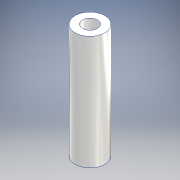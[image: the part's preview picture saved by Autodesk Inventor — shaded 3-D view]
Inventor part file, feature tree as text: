
AUTODESK INVENTOR PART (.ipt)
format: ipt  version: 2016 (Build 200138000, 138)  size: 95,744 bytes
history: native  units: mm
features: other x1, extrude x1, sketch x1
ambient origin geometry x8: Origin, YZ Plane, XZ Plane, XY Plane, X Axis, Y Axis, Z Axis, Center Point
bodies: Body1 (feature_tree)
feature tree (3):
  other  "ソリッド1"
  extrude  "押し出し1"  Depth=6.0mm
  sketch  "スケッチ1"
